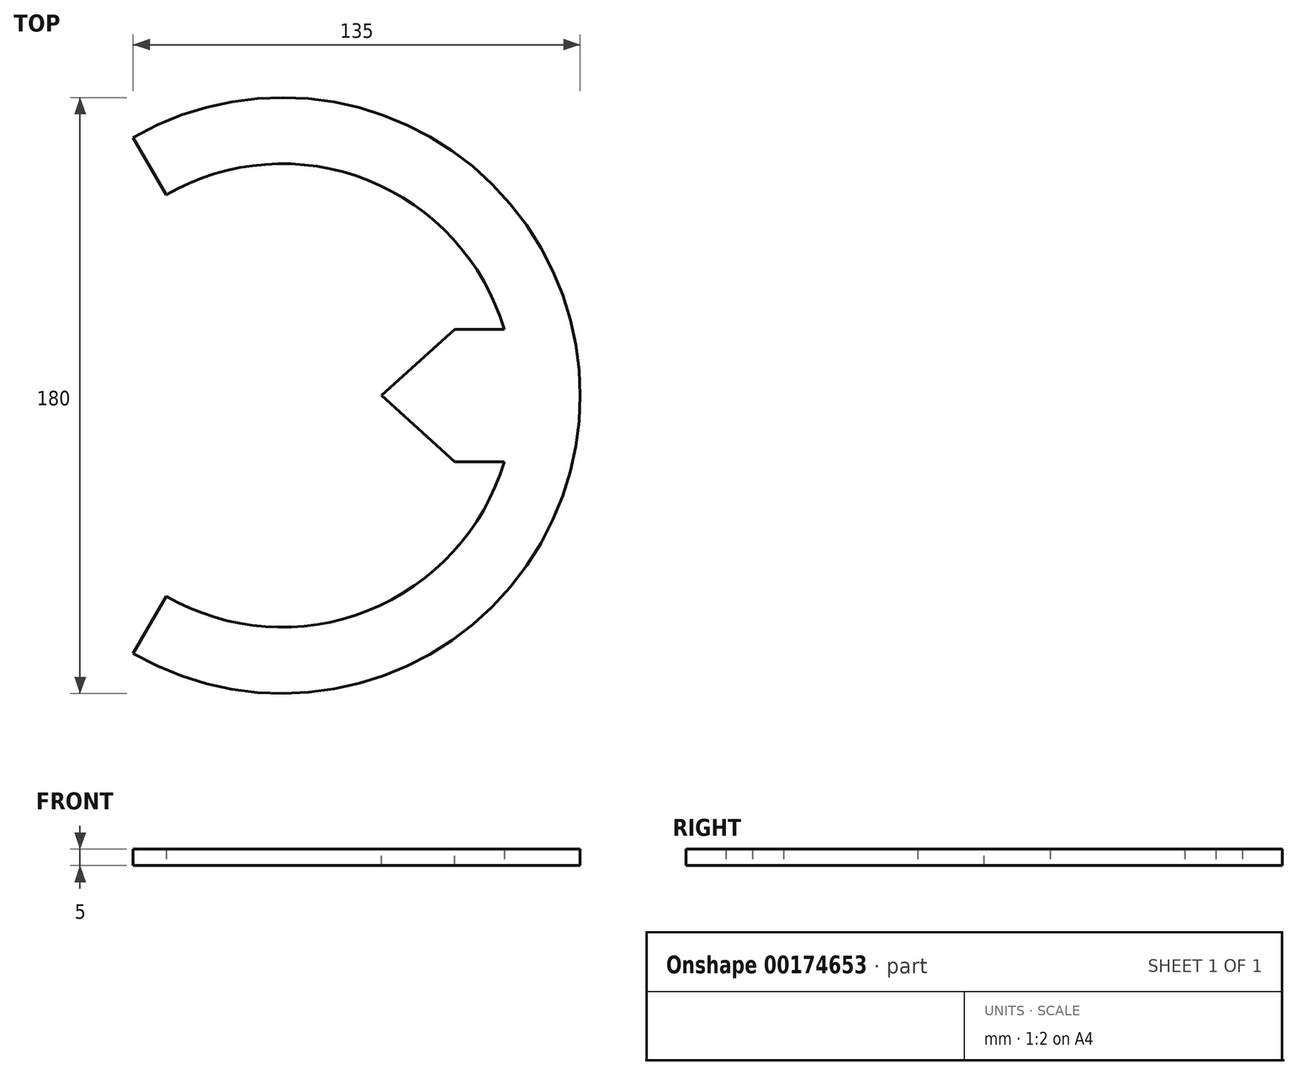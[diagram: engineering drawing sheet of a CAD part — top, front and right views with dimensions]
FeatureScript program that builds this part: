
annotation { "Feature Type Name" : "Feature", "Feature Type Description" : "" }
export const myFeature = defineFeature(function(context is Context, id is Id, definition is map)
    precondition{}
    {
        {
            var Q0;
            Q0=qCreatedBy(makeId("Top.planeOp"),FACE);
            var sketch = newSketch(context, id + "F0", { "sketchPlane" : qUnion([Q0])});
            skCircle(sketch, "E0", {"center": v(0, 0) * mm, "radius": 90 * mm});
            skSolve(sketch);
        }
        {
            var Q0;
            Q0=qCreatedBy(makeId("Top.planeOp"),FACE);
            var sketch = newSketch(context, id + "F1", { "sketchPlane" : qUnion([Q0])});
            skLineSegment(sketch, "E1", {"start": v(0, 0) * mm, "end": v(-90, 0) * mm, "construction": true});
            skLineSegment(sketch, "E2", {"start": v(-45, 77.94) * mm, "end": v(-35, 60.62) * mm});
            skArc(sketch, "E3", {"start": v(70, 0) * mm, "mid": v(35, 60.62) * mm, "end": v(-35, 60.62) * mm});
            skArc(sketch, "E4", {"start": v(90, 0) * mm, "mid": v(45, 77.94) * mm, "end": v(-45, 77.94) * mm});
            skLineSegment(sketch, "E5", {"start": v(70, 0) * mm, "end": v(90, 0) * mm, "construction": true});
            skLineSegment(sketch, "E6", {"start": v(-35, 60.62) * mm, "end": v(0, 0) * mm, "construction": true});
            skLineSegment(sketch, "E7.MirrorCS", {"start": v(-45, -77.94) * mm, "end": v(-35, -60.62) * mm});
            skArc(sketch, "E8.MirrorCS", {"start": v(90, 0) * mm, "mid": v(45, -77.94) * mm, "end": v(-45, -77.94) * mm});
            skArc(sketch, "E9.MirrorCS", {"start": v(70, 0) * mm, "mid": v(35, -60.62) * mm, "end": v(-35, -60.62) * mm});
            skSolve(sketch);
        }
        {
            var Q0;
            Q0 = qSketchRegion(id + "F1", true);
            var Q1;
            Q1=sQuery(id+"F1.wireOp",EDGE,"E5");
            extrude(context, id + "F2", {"entities" : qUnion([Q0]), "surfaceEntities" : qUnion([Q1]), "depth" : 5 * mm});
        }
        {
            var Q0;
            Q0=makeQuery(id+"F2.opExtrude","CAP_FACE",FACE,{"disambiguationData":[OSD([sQuery(id+"F1.wireOp",EDGE,"E2"),sQuery(id+"F1.wireOp",EDGE,"E3"),sQuery(id+"F1.wireOp",EDGE,"E4"),sQuery(id+"F1.wireOp",EDGE,"E7.MirrorCS"),sQuery(id+"F1.wireOp",EDGE,"E8.MirrorCS"),sQuery(id+"F1.wireOp",EDGE,"E9.MirrorCS")])],"isStart":false});
            var sketch = newSketch(context, id + "F3", { "sketchPlane" : qUnion([Q0])});
            skLineSegment(sketch, "E10", {"start": v(67.08, 20) * mm, "end": v(87.75, 20) * mm});
            skArc(sketch, "E11", {"start": v(67.08, -20) * mm, "mid": v(70, 0) * mm, "end": v(67.08, 20) * mm});
            skArc(sketch, "E12", {"start": v(87.75, -20) * mm, "mid": v(90, 0) * mm, "end": v(87.75, 20) * mm});
            skLineSegment(sketch, "E13.MirrorCS", {"start": v(67.08, -20) * mm, "end": v(87.75, -20) * mm});
            skLineSegment(sketch, "E14", {"start": v(30, 0) * mm, "end": v(52.08, 20) * mm});
            skPoint(sketch, "E14.startSnap0", {"position": v(70, 0) * mm});
            skLineSegment(sketch, "E15", {"start": v(52.08, 20) * mm, "end": v(67.08, 20) * mm});
            skLineSegment(sketch, "E16.MirrorCS", {"start": v(52.08, -20) * mm, "end": v(67.08, -20) * mm});
            skLineSegment(sketch, "E17.MirrorCS", {"start": v(30, 0) * mm, "end": v(52.08, -20) * mm});
            skSolve(sketch);
        }
        {
            var Q0;
            Q0 = qSketchRegion(id + "F3", true);
            var Q1;
            Q1=makeQuery(id+"F2.opExtrude","CAP_FACE",FACE,{"disambiguationData":[OSD([sQuery(id+"F1.wireOp",EDGE,"E2"),sQuery(id+"F1.wireOp",EDGE,"E3"),sQuery(id+"F1.wireOp",EDGE,"E4"),sQuery(id+"F1.wireOp",EDGE,"E7.MirrorCS"),sQuery(id+"F1.wireOp",EDGE,"E8.MirrorCS"),sQuery(id+"F1.wireOp",EDGE,"E9.MirrorCS")])],"isStart":true});
            extrude(context, id + "F4", {"entities" : qUnion([Q0]), "operationType" : NewBodyOperationType.ADD, "endBound" : BoundingType.UP_TO_SURFACE, "oppositeDirection" : true, "endBoundEntityFace" : qUnion([Q1]), "depth" : 25 * mm});
        }
    });
